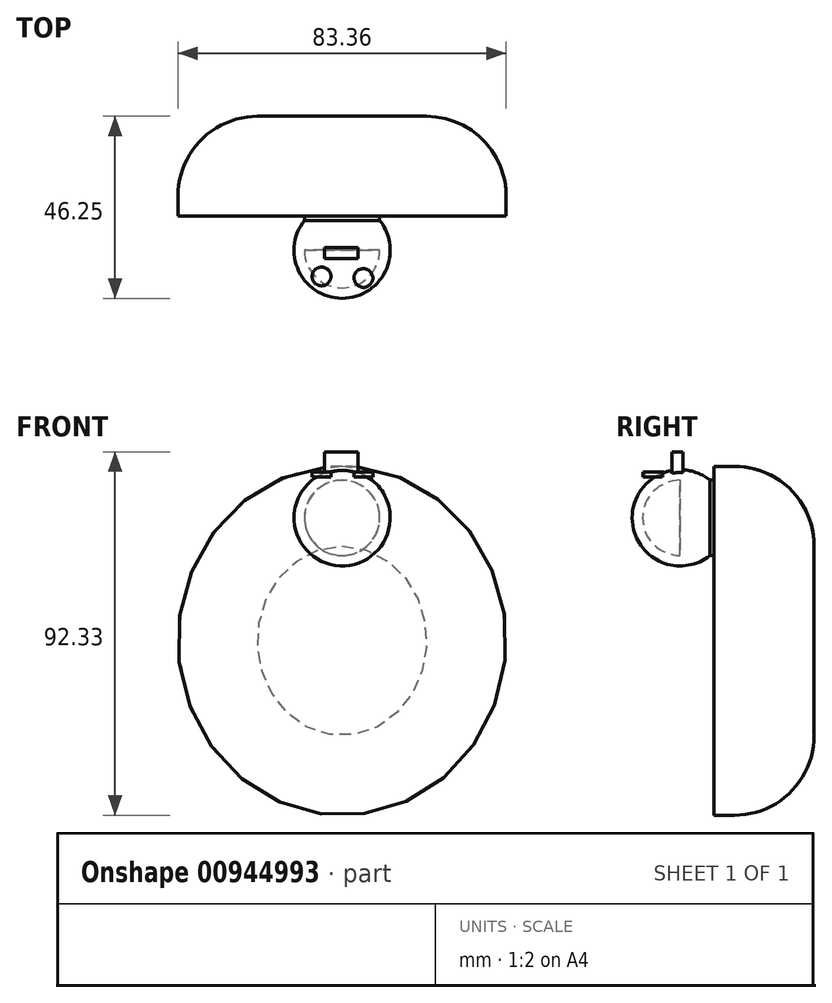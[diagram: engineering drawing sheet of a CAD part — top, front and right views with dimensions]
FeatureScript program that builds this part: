
annotation { "Feature Type Name" : "Feature", "Feature Type Description" : "" }
export const myFeature = defineFeature(function(context is Context, id is Id, definition is map)
    precondition{}
    {
        {
            var Q0;
            Q0=qCreatedBy(makeId("Front.planeOp"),FACE);
            var sketch = newSketch(context, id + "F0", { "sketchPlane" : qUnion([Q0])});
            skEllipse(sketch, "E0", {"center": v(0, 0) * mm, "majorRadius": 41.68 * mm, "minorRadius": 44.32 * mm, "majorAxis": v(1, 0)});
            skSolve(sketch);
        }
        {
            var Q0;
            Q0 = qSketchRegion(id + "F0", true);
            extrude(context, id + "F1", {"entities" : qUnion([Q0]), "depth" : 25.4 * mm, "offsetDistance" : 25.4 * mm});
        }
        {
            var Q0;
            Q0=makeQuery(id+"F1.opExtrude","CAP_FACE",FACE,{"disambiguationData":[OSD([sQuery(id+"F0.wireOp",EDGE,"E0")])],"isStart":true});
            fillet(context, id + "F2", {"entities" : qUnion([Q0]), "radius" : 20.24 * mm, "tangentPropagation" : true, "allowEdgeOverflow" : false});
        }
        {
            var Q0;
            Q0=makeQuery(id+"F1.opExtrude","CAP_FACE",FACE,{"disambiguationData":[OSD([sQuery(id+"F0.wireOp",EDGE,"E0")])],"isStart":false});
            var sketch = newSketch(context, id + "F3", { "sketchPlane" : qUnion([Q0])});
            skCircle(sketch, "E1", {"center": v(0, 31.24) * mm, "radius": 9.56 * mm});
            skSolve(sketch);
        }
        {
            var Q0;
            Q0=makeQuery(id+"F3.imprint","IMPRINT",FACE,{"disambiguationData":[TD([[makeQuery(id+"F3.imprint","IMPRINT",EDGE,{"derivedFrom":sQuery(id+"F3.wireOp",EDGE,"E1")}),1.0]])]});
            extrude(context, id + "F4", {"entities" : qUnion([Q0]), "operationType" : NewBodyOperationType.ADD, "depth" : 8.64 * mm, "offsetDistance" : 25.4 * mm});
        }
        {
            var Q0;
            Q0=makeQuery(id+"F4.opExtrude","CAP_FACE",FACE,{"disambiguationData":[OSD([sQuery(id+"F3.wireOp",EDGE,"E1")])],"isStart":false});
            var sketch = newSketch(context, id + "F5", { "sketchPlane" : qUnion([Q0])});
            skCircle(sketch, "E2", {"center": v(0, 31.24) * mm, "radius": 12.21 * mm});
            skLineSegment(sketch, "E3", {"start": v(12.2, 31.92) * mm, "end": v(0, 31.24) * mm});
            skLineSegment(sketch, "E4", {"start": v(0, 31.24) * mm, "end": v(-12.2, 30.55) * mm});
            skSolve(sketch);
        }
        {
            var Q0;
            {var subQ0=sQuery(id+"F5.wireOp",EDGE,"E3");var subQ1=sQuery(id+"F5.wireOp",EDGE,"E2");var subQ2=makeQuery(id+"F5.imprint","INTERSECT",VERTEX,{"derivedFrom":[subQ1,subQ0]});Q0=makeQuery(id+"F5.imprint","IMPRINT",FACE,{"disambiguationData":[TD([[makeQuery(id+"F5.imprint","IMPRINT",EDGE,{"disambiguationData":[TD([[subQ2,1.0]])],"derivedFrom":subQ1}),1.0]])]});}
            var Q1;
            Q1=sQuery(id+"F5.wireOp",EDGE,"E4");
            revolve(context, id + "F6", {"operationType" : NewBodyOperationType.ADD, "surfaceOperationType" : NewSurfaceOperationType.NEW, "entities" : qUnion([Q0]), "axis" : qUnion([Q1]), "revolveType" : RevolveType.FULL});
        }
        {
            var Q0;
            Q0=qCreatedBy(makeId("Top.planeOp"),FACE);
            cPlane(context, id + "F7", {"entities" : qUnion([Q0]), "cplaneType" : CPlaneType.OFFSET, "offset" : 41.66 * mm, "width" : 152.4 * mm, "height" : 152.4 * mm});
        }
        {
            var Q0;
            Q0=qCreatedBy(id+"F7.planeOp",FACE);
            var sketch = newSketch(context, id + "F8", { "sketchPlane" : qUnion([Q0])});
            skLineSegment(sketch, "E5.bottom", {"start": v(-4.43, -33.4) * mm, "end": v(4.04, -33.4) * mm});
            skLineSegment(sketch, "E5.top", {"start": v(-4.43, -36.16) * mm, "end": v(4.04, -36.16) * mm});
            skLineSegment(sketch, "E5.left", {"start": v(-4.43, -33.4) * mm, "end": v(-4.43, -36.16) * mm});
            skLineSegment(sketch, "E5.right", {"start": v(4.04, -33.4) * mm, "end": v(4.04, -36.16) * mm});
            skSolve(sketch);
        }
        {
            var Q0;
            Q0 = qSketchRegion(id + "F8", true);
            extrude(context, id + "F9", {"entities" : qUnion([Q0]), "operationType" : NewBodyOperationType.ADD, "depth" : 6.35 * mm, "offsetDistance" : 25.4 * mm});
        }
        {
            var Q0;
            Q0=qCreatedBy(id+"F7.planeOp",FACE);
            var sketch = newSketch(context, id + "F10", { "sketchPlane" : qUnion([Q0])});
            skCircle(sketch, "E6", {"center": v(-5.22, -40.7) * mm, "radius": 2.38 * mm});
            skCircle(sketch, "E7", {"center": v(5.42, -41.09) * mm, "radius": 2.38 * mm});
            skSolve(sketch);
        }
        {
            var Q0;
            Q0 = qSketchRegion(id + "F10", true);
            extrude(context, id + "F11", {"entities" : qUnion([Q0]), "operationType" : NewBodyOperationType.ADD, "depth" : 1.27 * mm, "offsetDistance" : 25.4 * mm});
        }
    });
